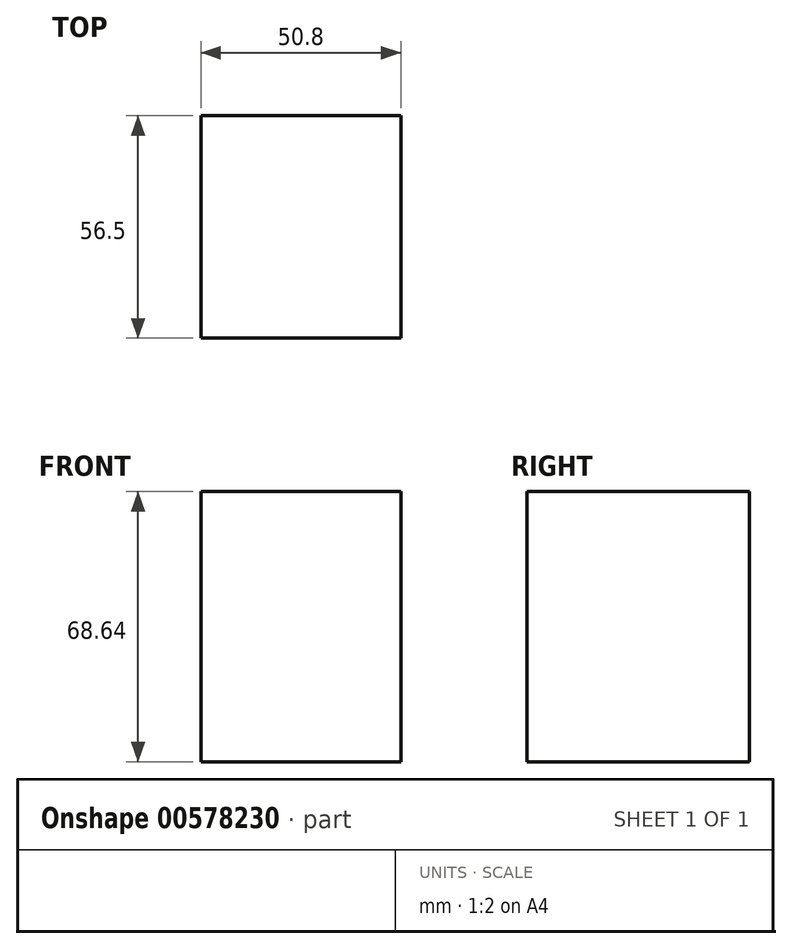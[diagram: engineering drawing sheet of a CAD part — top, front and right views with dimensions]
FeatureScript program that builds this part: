
annotation { "Feature Type Name" : "Feature", "Feature Type Description" : "" }
export const myFeature = defineFeature(function(context is Context, id is Id, definition is map)
    precondition{}
    {
        {
            var Q0;
            Q0=qCreatedBy(makeId("Right.planeOp"),FACE);
            var sketch = newSketch(context, id + "F0", { "sketchPlane" : qUnion([Q0])});
            skLineSegment(sketch, "E0.bottom", {"start": v(-28.25, 34.32) * mm, "end": v(28.25, 34.32) * mm});
            skLineSegment(sketch, "E0.top", {"start": v(-28.25, -34.32) * mm, "end": v(28.25, -34.32) * mm});
            skLineSegment(sketch, "E0.left", {"start": v(-28.25, 34.32) * mm, "end": v(-28.25, -34.32) * mm});
            skLineSegment(sketch, "E0.right", {"start": v(28.25, 34.32) * mm, "end": v(28.25, -34.32) * mm});
            skPoint(sketch, "E0.middle", {"position": v(0, 0) * mm});
            skSolve(sketch);
        }
        {
            var Q0;
            Q0 = qSketchRegion(id + "F0", true);
            extrude(context, id + "F1", {"entities" : qUnion([Q0]), "depth" : 50.8 * mm, "offsetDistance" : 25.4 * mm});
        }
    });
